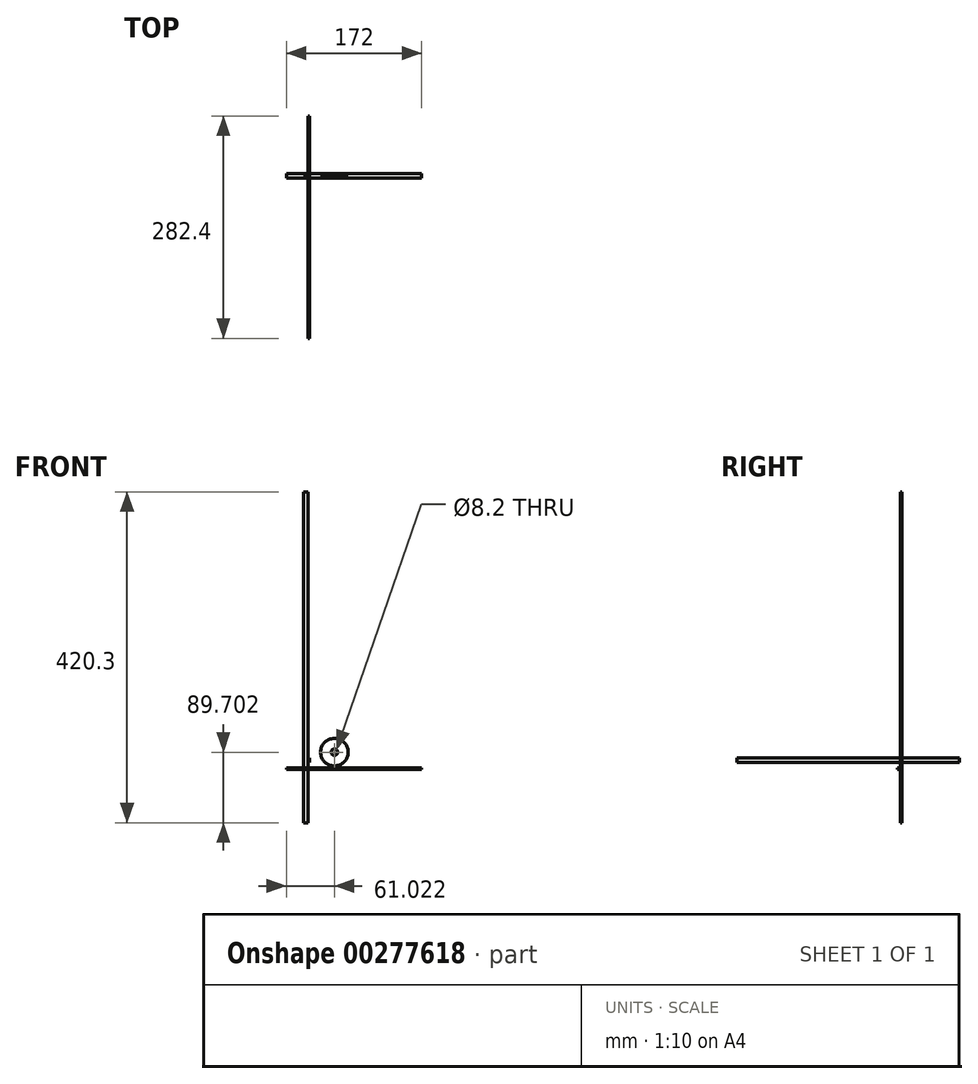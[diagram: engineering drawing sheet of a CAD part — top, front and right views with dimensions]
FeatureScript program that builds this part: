
annotation { "Feature Type Name" : "Feature", "Feature Type Description" : "" }
export const myFeature = defineFeature(function(context is Context, id is Id, definition is map)
    precondition{}
    {
        {
            var Q0;
            Q0=qCreatedBy(makeId("Front.planeOp"),FACE);
            var sketch = newSketch(context, id + "F0", { "sketchPlane" : qUnion([Q0])});
            skLineSegment(sketch, "E0.bottom", {"start": v(-27.73, 2) * mm, "end": v(144.27, 2) * mm});
            skLineSegment(sketch, "E0.top", {"start": v(-27.73, 0) * mm, "end": v(144.27, 0) * mm});
            skLineSegment(sketch, "E0.left", {"start": v(-27.73, 2) * mm, "end": v(-27.73, 0) * mm});
            skLineSegment(sketch, "E0.right", {"start": v(144.27, 2) * mm, "end": v(144.27, 0) * mm});
            skSolve(sketch);
        }
        {
            var Q0;
            Q0=makeQuery(id+"F0.imprint","IMPRINT",FACE,{"disambiguationData":[TD([[makeQuery(id+"F0.imprint","IMPRINT",EDGE,{"derivedFrom":sQuery(id+"F0.wireOp",EDGE,"E0.bottom")}),-1.0]])]});
            extrude(context, id + "F1", {"entities" : qUnion([Q0]), "depth" : 6 * mm});
        }
        {
            var Q0;
            Q0=qCreatedBy(makeId("Right.planeOp"),FACE);
            var sketch = newSketch(context, id + "F2", { "sketchPlane" : qUnion([Q0])});
            skLineSegment(sketch, "E1.bottom", {"start": v(-209.45, 14.64) * mm, "end": v(72.95, 14.64) * mm});
            skLineSegment(sketch, "E1.top", {"start": v(-209.45, 8.64) * mm, "end": v(72.95, 8.64) * mm});
            skLineSegment(sketch, "E1.left", {"start": v(-209.45, 14.64) * mm, "end": v(-209.45, 8.64) * mm});
            skLineSegment(sketch, "E1.right", {"start": v(72.95, 14.64) * mm, "end": v(72.95, 8.64) * mm});
            skSolve(sketch);
        }
        {
            var Q0;
            Q0=makeQuery(id+"F2.imprint","IMPRINT",FACE,{"disambiguationData":[TD([[makeQuery(id+"F2.imprint","IMPRINT",EDGE,{"derivedFrom":sQuery(id+"F2.wireOp",EDGE,"E1.bottom")}),-1.0]])]});
            extrude(context, id + "F3", {"entities" : qUnion([Q0]), "depth" : 2 * mm});
        }
        {
            var Q0;
            Q0=qCreatedBy(makeId("Front.planeOp"),FACE);
            var sketch = newSketch(context, id + "F4", { "sketchPlane" : qUnion([Q0])});
            skLineSegment(sketch, "E2.bottom", {"start": v(0, 352.38) * mm, "end": v(-6, 352.38) * mm});
            skLineSegment(sketch, "E2.top", {"start": v(0, -67.92) * mm, "end": v(-6, -67.92) * mm});
            skLineSegment(sketch, "E2.left", {"start": v(0, 352.38) * mm, "end": v(0, -67.92) * mm});
            skLineSegment(sketch, "E2.right", {"start": v(-6, 352.38) * mm, "end": v(-6, -67.92) * mm});
            skSolve(sketch);
        }
        {
            var Q0;
            Q0=makeQuery(id+"F4.imprint","IMPRINT",FACE,{"disambiguationData":[TD([[makeQuery(id+"F4.imprint","IMPRINT",EDGE,{"derivedFrom":sQuery(id+"F4.wireOp",EDGE,"E2.bottom")}),1.0]])]});
            extrude(context, id + "F5", {"entities" : qUnion([Q0]), "depth" : 2 * mm});
        }
        {
            var Q0;
            Q0=qCreatedBy(makeId("Front.planeOp"),FACE);
            var sketch = newSketch(context, id + "F6", { "sketchPlane" : qUnion([Q0])});
            skCircle(sketch, "E3", {"center": v(33.3, 21.78) * mm, "radius": 17.5 * mm});
            skCircle(sketch, "E4", {"center": v(33.3, 21.78) * mm, "radius": 4.1 * mm});
            skSolve(sketch);
        }
        {
            var Q0;
            Q0=makeQuery(id+"F6.imprint","IMPRINT",FACE,{"disambiguationData":[TD([[makeQuery(id+"F6.imprint","IMPRINT",EDGE,{"derivedFrom":sQuery(id+"F6.wireOp",EDGE,"E3")}),1.0]])]});
            extrude(context, id + "F7", {"entities" : qUnion([Q0]), "depth" : 2 * mm});
        }
    });
